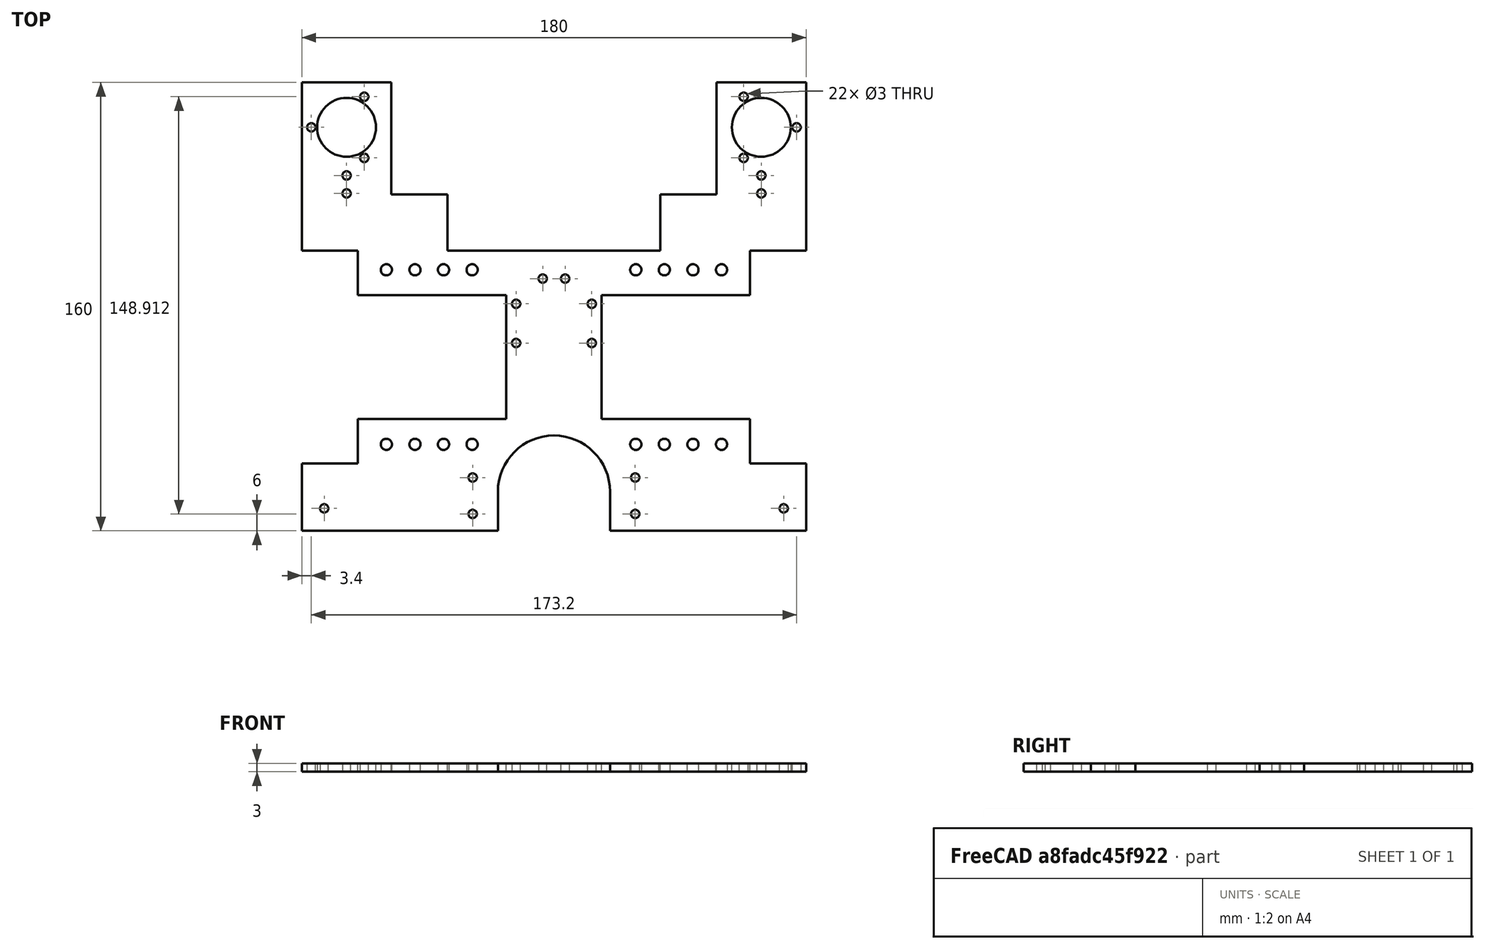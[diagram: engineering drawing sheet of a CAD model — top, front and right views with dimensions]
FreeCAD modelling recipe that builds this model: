
FCSTD DOCUMENT  (FreeCAD 0.16R6707 (Git))
Label: base
License: All rights reserved
LicenseURL: http://en.wikipedia.org/wiki/All_rights_reserved
objects: Sketcher::SketchObject×1, PartDesign::Pad×1, PartDesign::Mirrored×1
note: 4 computed .brp shape members not serialized (recipe doc carries the construction recipe); baked Part::Feature solids carry a one-line shape summary decoded from their .brp

FEATURE [Sketcher::SketchObject] Sketch
  sketch-geometry (63):
    g0: LineSegment StartX=0 StartY=0 StartZ=0 EndX=0 EndY=24 EndZ=0
    g1: LineSegment StartX=0 StartY=24 StartZ=0 EndX=20 EndY=24 EndZ=0
    g2: LineSegment StartX=20 StartY=24 StartZ=0 EndX=20 EndY=39.85 EndZ=0
    g3: LineSegment StartX=20 StartY=39.85 StartZ=0 EndX=73 EndY=39.85 EndZ=0
    g4: LineSegment StartX=73 StartY=39.85 StartZ=0 EndX=73 EndY=84.15 EndZ=0
    g5: LineSegment StartX=73 StartY=84.15 StartZ=0 EndX=20 EndY=84.15 EndZ=0
    g6: LineSegment StartX=20 StartY=84.15 StartZ=0 EndX=20 EndY=100 EndZ=0
    g7: LineSegment StartX=20 StartY=100 StartZ=0 EndX=0 EndY=100 EndZ=0
    g8: LineSegment StartX=0 StartY=100 StartZ=0 EndX=0 EndY=160 EndZ=0
    g9: LineSegment StartX=0 StartY=160 StartZ=0 EndX=32 EndY=160 EndZ=0
    g10: LineSegment StartX=0 StartY=0 StartZ=0 EndX=70 EndY=0 EndZ=0
    g11: LineSegment StartX=70 StartY=0 StartZ=0 EndX=70 EndY=14 EndZ=0
    g12: GeomPoint [constr] X=16 Y=144 Z=0
    g13: Circle CenterX=16 CenterY=144 CenterZ=0 NormalX=0 NormalY=0 NormalZ=1 Radius=10.5
    g14: GeomPoint [constr] X=22.3 Y=154.912 Z=0
    g15: GeomPoint [constr] X=22.3 Y=133.088 Z=0
    g16: GeomPoint [constr] X=3.4 Y=144 Z=0
    g17: Circle CenterX=22.3 CenterY=154.912 CenterZ=0 NormalX=0 NormalY=0 NormalZ=1 Radius=1.5
    g18: Circle CenterX=22.3 CenterY=133.088 CenterZ=0 NormalX=0 NormalY=0 NormalZ=1 Radius=1.5
    g19: Circle CenterX=3.4 CenterY=144 CenterZ=0 NormalX=0 NormalY=0 NormalZ=1 Radius=1.5
    g20: GeomPoint [constr] X=30.2 Y=93.15 Z=0
    g21: GeomPoint [constr] X=40.4 Y=93.15 Z=0
    g22: GeomPoint [constr] X=50.6 Y=93.15 Z=0
    g23: GeomPoint [constr] X=60.8 Y=93.15 Z=0
    g24: GeomPoint [constr] X=30.2 Y=30.85 Z=0
    g25: GeomPoint [constr] X=40.4 Y=30.85 Z=0
    g26: GeomPoint [constr] X=50.6 Y=30.85 Z=0
    g27: GeomPoint [constr] X=60.8 Y=30.85 Z=0
    g28: Circle CenterX=30.2 CenterY=30.85 CenterZ=0 NormalX=0 NormalY=0 NormalZ=1 Radius=2
    g29: Circle CenterX=40.4 CenterY=30.85 CenterZ=0 NormalX=0 NormalY=0 NormalZ=1 Radius=2
    g30: Circle CenterX=50.6 CenterY=30.85 CenterZ=0 NormalX=0 NormalY=0 NormalZ=1 Radius=2
    g31: Circle CenterX=60.8 CenterY=30.85 CenterZ=0 NormalX=0 NormalY=0 NormalZ=1 Radius=2
    g32: Circle CenterX=30.2 CenterY=93.15 CenterZ=0 NormalX=0 NormalY=0 NormalZ=1 Radius=2
    g33: Circle CenterX=40.4 CenterY=93.15 CenterZ=0 NormalX=0 NormalY=0 NormalZ=1 Radius=2
    g34: Circle CenterX=50.6 CenterY=93.15 CenterZ=0 NormalX=0 NormalY=0 NormalZ=1 Radius=2
    g35: Circle CenterX=60.8 CenterY=93.15 CenterZ=0 NormalX=0 NormalY=0 NormalZ=1 Radius=2
    g36: GeomPoint [constr] X=76.5 Y=74 Z=0
    g37: GeomPoint [constr] X=76.5 Y=81 Z=0
    g38: GeomPoint [constr] X=76.5 Y=67 Z=0
    g39: Circle CenterX=76.5 CenterY=81 CenterZ=0 NormalX=0 NormalY=0 NormalZ=1 Radius=1.5
    g40: Circle CenterX=76.5 CenterY=67 CenterZ=0 NormalX=0 NormalY=0 NormalZ=1 Radius=1.5
    g41: GeomPoint [constr] X=61 Y=19 Z=0
    g42: GeomPoint [constr] X=61 Y=6 Z=0
    g43: Circle CenterX=61 CenterY=19 CenterZ=0 NormalX=0 NormalY=0 NormalZ=1 Radius=1.5
    g44: Circle CenterX=61 CenterY=6 CenterZ=0 NormalX=0 NormalY=0 NormalZ=1 Radius=1.5
    g45: GeomPoint [constr] X=8 Y=8 Z=0
    g46: Circle CenterX=8 CenterY=8 CenterZ=0 NormalX=0 NormalY=0 NormalZ=1 Radius=1.5
    g47: LineSegment StartX=52 StartY=100 StartZ=0 EndX=90 EndY=100 EndZ=0
    g48: LineSegment StartX=90 StartY=100 StartZ=0 EndX=90 EndY=34 EndZ=0
    g49: GeomPoint [constr] X=90 Y=14 Z=0
    g50: ArcOfCircle CenterX=90 CenterY=14 CenterZ=0 NormalX=0 NormalY=0 NormalZ=1 Radius=20 StartAngle=1.5708 EndAngle=3.14159
    g51: GeomPoint [constr] X=86 Y=90 Z=0
    g52: Circle CenterX=86 CenterY=90 CenterZ=0 NormalX=0 NormalY=0 NormalZ=1 Radius=1.5
    g53: LineSegment StartX=52 StartY=100 StartZ=0 EndX=52 EndY=120 EndZ=0
    g54: LineSegment StartX=52 StartY=120 StartZ=0 EndX=32 EndY=120 EndZ=0
    g55: LineSegment StartX=32 StartY=160 StartZ=0 EndX=32 EndY=120 EndZ=0
    g56: GeomPoint [constr] X=16 Y=146 Z=0
    g57: GeomPoint [constr] X=16 Y=139.6 Z=0
    g58: GeomPoint [constr] X=16 Y=126.8 Z=0
    g59: GeomPoint [constr] X=16 Y=120.4 Z=0
    g60: GeomPoint [constr] X=16 Y=133.2 Z=0
    g61: Circle CenterX=16 CenterY=126.8 CenterZ=0 NormalX=0 NormalY=0 NormalZ=1 Radius=1.5
    g62: Circle CenterX=16 CenterY=120.4 CenterZ=0 NormalX=0 NormalY=0 NormalZ=1 Radius=1.5
  constraints (134):
    c: Coincident(g0,g-1)
    c: Vertical(g0)
    c: Coincident(g1,g0)
    c: Horizontal(g1)
    c: Coincident(g2,g1)
    c: Vertical(g2)
    c: Coincident(g3,g2)
    c: Horizontal(g3)
    c: Coincident(g4,g3)
    c: Vertical(g4)
    c: Coincident(g5,g4)
    c: Horizontal(g5)
    c: Coincident(g6,g5)
    c: Vertical(g6)
    c: Coincident(g7,g6)
    c: Horizontal(g7)
    c: Distance(g0) = 24
    c: Distance(g1) = 20
    c: Distance(g2) = 15.85
    c: Distance(g3) = 53
    c: Distance(g4) = 44.3
    c: Distance(g5) = 53
    c: Distance(g6) = 15.85
    c: Distance(g7) = 20
    c: Coincident(g8,g7)
    c: Vertical(g8)
    c: Distance(g8) = 60
    c: Coincident(g9,g8)
    c: Horizontal(g9)
    c: Coincident(g10,g-1)
    c: Horizontal(g10)
    c: Distance(g10) = 70
    c: Coincident(g11,g10)
    c: Vertical(g11)
    c: Distance(g11) = 14
    c: DistanceX(g8,g12) = 16
    c: DistanceY(g12,g8) = 16
    c: Coincident(g13,g12)
    c: Radius(g13) = 10.5
    c: Coincident(g17,g14)
    c: Coincident(g18,g15)
    c: Coincident(g19,g16)
    c: Radius(g17) = 1.5
    c: Equal(g17,g18)
    c: Equal(g17,g19)
    c: DistanceY(g5,g20) = 9
    c: DistanceX(g5,g20) = 10.2
    c: DistanceX(g20,g21) = 10.2
    c: DistanceX(g21,g22) = 10.2
    c: DistanceX(g22,g23) = 10.2
    c: DistanceY(g20,g21) = 0
    c: DistanceY(g21,g22) = 0
    c: DistanceY(g23,g22) = 0
    c: DistanceY(g25,g24) = 0
    c: DistanceX(g24,g25) = 10.2
    c: DistanceX(g25,g26) = 10.2
    c: DistanceX(g26,g27) = 10.2
    c: DistanceY(g26,g25) = 0
    c: DistanceY(g27,g26) = 0
    c: DistanceX(g2,g24) = 10.2
    c: DistanceY(g24,g2) = 9
    c: Coincident(g28,g24)
    c: Coincident(g29,g25)
    c: Coincident(g30,g26)
    c: Coincident(g31,g27)
    c: Coincident(g32,g20)
    c: Coincident(g33,g21)
    c: Coincident(g34,g22)
    c: Coincident(g35,g23)
    c: Radius(g32) = 2
    c: Equal(g32,g33)
    c: Equal(g32,g34)
    c: Equal(g32,g35)
    c: Equal(g32, g28-g31) x4
    c: DistanceY(g36) = 74
    c: DistanceX(g36,g48) = 13.5
    c: DistanceY(g38,g36) = 7
    c: DistanceY(g36,g37) = 7
    c: DistanceX(g37,g36) = 0
    c: DistanceX(g36,g38) = 0
    c: Coincident(g39,g37)
    c: Coincident(g40,g38)
    c: Radius(g40) = 1.5
    c: Equal(g40,g39)
    c: DistanceX(g42,g10) = 9
    c: DistanceY(g42) = 6
    c: DistanceY(g42,g41) = 13
    c: DistanceX(g42,g41) = 0
    c: Coincident(g43,g41)
    c: Coincident(g44,g42)
    c: Radius(g43) = 1.5
    c: Equal(g43,g44)
    c: DistanceY(g-1,g45) = 8
    c: DistanceX(g45) = 8
    c: Coincident(g46,g45)
    c: Radius(g46) = 1.5
    c: Horizontal(g47)
    c: Coincident(g48,g47)
    c: DistanceY(g48) = 34
    c: DistanceX(g48) = 90
    c: DistanceY(g11,g49) = 0
    c: DistanceX(g49,g48) = 0
    c: Coincident(g50,g49)
    c: Coincident(g50,g48)
    c: Coincident(g50,g11)
    c: DistanceY(g48,g51) = 56
    c: DistanceX(g51,g47) = 4
    c: Coincident(g52,g51)
    c: Radius(g52) = 1.5
    c: DistanceX(g47) = 90
    c: Distance(g47) = 38
    c: Coincident(g53,g47)
    c: Vertical(g53)
    c: Coincident(g54,g53)
    c: Horizontal(g54)
    c: Distance(g9) = 32
    c: Distance(g54) = 20
    c: Coincident(g55,g9)
    c: Coincident(g55,g54)
    c: Distance(g55) = 40
    c: DistanceY(g56,g8) = 14
    c: DistanceX(g56) = 16
    c: DistanceY(g57,g56) = 6.4
    c: DistanceY(g60,g57) = 6.4
    c: DistanceY(g58,g60) = 6.4
    c: DistanceY(g59,g58) = 6.4
    c: DistanceX(g57,g56) = 0
    c: DistanceX(g60,g57) = 0
    c: DistanceX(g58,g60) = 0
    c: DistanceX(g59,g58) = 0
    c: Coincident(g61,g58)
    c: Coincident(g62,g59)
    c: Radius(g62) = 1.5
    c: Equal(g62,g61)
FEATURE [PartDesign::Pad] Pad
  Length = 3
  Length2 = 100
  Sketch = -> Sketch
  Type = 0
FEATURE [PartDesign::Mirrored] Mirrored
  MirrorPlane = -> Pad [Face2]
  Originals = -> [Pad]
